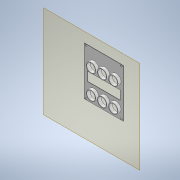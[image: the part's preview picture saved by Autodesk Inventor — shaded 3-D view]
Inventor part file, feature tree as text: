
AUTODESK INVENTOR PART (.ipt)
format: ipt  version: 2022 (Build 260153000, 153)  size: 176,128 bytes
history: native  units: mm
features: other x10, reference x8, extrude x2, sketch x2, plane x1, projected_geometry x1
ambient origin geometry x8: Origin, YZ Plane, XZ Plane, XY Plane, X Axis, Y Axis, Z Axis, Center Point
bodies: Solid1 (feature_tree)
feature tree (24):
  plane  "Work Plane1"
  extrude  "Extrusion1"  Depth=0.2mm
  extrude  "Extrusion2"  Depth=10.0mm
  sketch  "Sketch1"  dims[d0=0.2mm d1=0.2mm]
  reference  "Reference1"
  reference  "Reference2"
  reference  "Reference3"
  reference  "Reference4"
  reference  "Reference5"
  reference  "Reference6"
  reference  "Reference7"
  reference  "Reference8"
  sketch  "Sketch2"  dims[d2=0.2mm d3=0.2mm d4=0.2mm d5=0.2mm d6=0.0mm d7=1.0mm d8=0.0mm d9=2.0mm d10=2.0mm d11=2.0mm d12=2.0mm d13=2.0mm d14=2.0mm d15=10.0mm d16=0.0mm d17=25.0mm d18=25.0mm d19=10.0mm d20=10.0mm]
  projected_geometry  "Projected Loop1"
  other  "<userpath>\OneDrive - Imperial College London\ROBOICP\Final Assembly\Final Assembly.iam"
  other  "Final Assembly.iam"
  other  "vial:1"
  other  "vial:3"
  other  "vial:5"
  other  "vial:2"
  other  "vial:4"
  other  "vial:6"
  other  "Reaction Printer:1"
  other  "Bed_Surface_v3:1"
